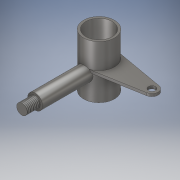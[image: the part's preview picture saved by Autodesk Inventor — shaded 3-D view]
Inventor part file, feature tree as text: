
AUTODESK INVENTOR PART (.ipt)
format: ipt  version: 2019 (Build 230136000, 136)  size: 189,440 bytes
history: native  units: mm
features: extrude x5, sketch x4, plane x3, projected_geometry x2, thread x1
ambient origin geometry x8: Origin, YZ Plane, XZ Plane, XY Plane, X Axis, Y Axis, Z Axis, Center Point
bodies: Solid1 (feature_tree)
feature tree (15):
  extrude  "Extrusion1"  Depth=30.0mm
  plane  "Work Plane4"
  sketch  "Sketch2"  dims[d2=60.0mm d3=0.0mm d4=17.5mm]
  extrude  "Extrusion2"  Depth=17.5mm
  extrude  "Extrusion3"  Depth=25.0mm
  extrude  "Extrusion4"  Depth=3.0mm TaperAngle=0.0deg
  thread  "Thread1"  [1 undecoded]
  plane  "Work Plane5"
  plane  "Work Plane6"
  extrude  "Extrusion5"  Depth=3.0mm TaperAngle=0.0deg
  sketch  "Sketch1"  dims[d0=35.0mm d1=30.0mm]
  projected_geometry  "Projected Loop1"
  sketch  "Sketch3"  dims[d5=17.0mm d6=25.0mm]
  projected_geometry  "Projected Loop2"
  sketch  "Sketch7"  dims[d7=55.0mm d8=0.0mm d9=70.0mm d10=0.0mm d11=12.0mm d12=15.0mm d13=0.0mm d14=15.0mm d15=0.0mm d23=9.599311mm d35=14.0mm d36=60.0mm d37=8.0mm d38=3.0mm d39=0.0mm]
note: 1 required parameter value undecoded (feature->parameter linkage not recoverable at this tier; creation-order binding heuristic only, values carry confidence <= 0.55)
